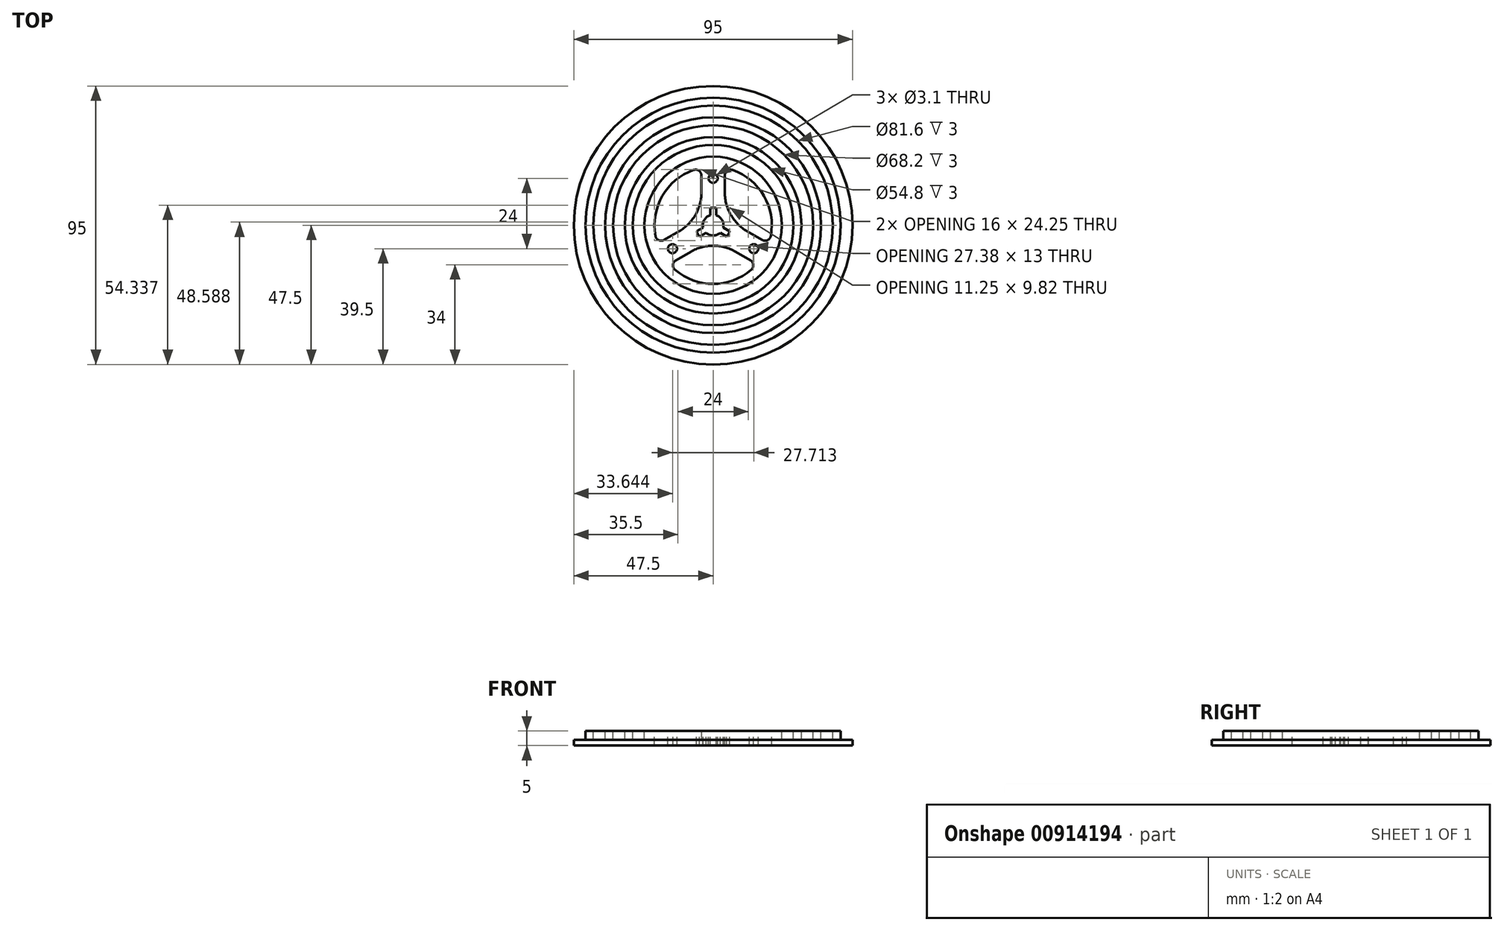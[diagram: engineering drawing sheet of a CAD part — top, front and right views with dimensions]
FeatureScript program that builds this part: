
annotation { "Feature Type Name" : "Feature", "Feature Type Description" : "" }
export const myFeature = defineFeature(function(context is Context, id is Id, definition is map)
    precondition{}
    {
        {
            var Q0;
            Q0=qCreatedBy(makeId("Front.planeOp"),FACE);
            var sketch = newSketch(context, id + "F0", { "sketchPlane" : qUnion([Q0])});
            skLineSegment(sketch, "E0", {"start": v(0, 9.24) * mm, "end": v(0, -8.58) * mm, "construction": true});
            skLineSegment(sketch, "E1", {"start": v(47.5, 0) * mm, "end": v(47.5, 2) * mm});
            skLineSegment(sketch, "E2", {"start": v(47.5, 2) * mm, "end": v(43.5, 2) * mm});
            skLineSegment(sketch, "E3", {"start": v(43.5, 2) * mm, "end": v(43.5, 5) * mm});
            skLineSegment(sketch, "E4", {"start": v(43.5, 5) * mm, "end": v(40.8, 5) * mm});
            skLineSegment(sketch, "E5", {"start": v(40.8, 5) * mm, "end": v(40.8, 2) * mm});
            skLineSegment(sketch, "E6", {"start": v(40.8, 2) * mm, "end": v(36.8, 2) * mm});
            skLineSegment(sketch, "E7", {"start": v(36.8, 2) * mm, "end": v(36.8, 5) * mm});
            skLineSegment(sketch, "E8", {"start": v(36.8, 5) * mm, "end": v(34.1, 5) * mm});
            skLineSegment(sketch, "E9", {"start": v(34.1, 5) * mm, "end": v(34.1, 2) * mm});
            skLineSegment(sketch, "E10", {"start": v(34.1, 2) * mm, "end": v(30.1, 2) * mm});
            skLineSegment(sketch, "E11", {"start": v(30.1, 2) * mm, "end": v(30.1, 5) * mm});
            skLineSegment(sketch, "E12", {"start": v(30.1, 5) * mm, "end": v(27.4, 5) * mm});
            skLineSegment(sketch, "E13", {"start": v(27.4, 5) * mm, "end": v(27.4, 2) * mm});
            skLineSegment(sketch, "E14", {"start": v(27.4, 2) * mm, "end": v(23.4, 2) * mm});
            skLineSegment(sketch, "E15", {"start": v(23.4, 2) * mm, "end": v(23.4, 5) * mm});
            skLineSegment(sketch, "E16", {"start": v(23.4, 5) * mm, "end": v(0, 5) * mm});
            skLineSegment(sketch, "E17", {"start": v(0, 5) * mm, "end": v(0, 0) * mm});
            skLineSegment(sketch, "E18", {"start": v(0, 0) * mm, "end": v(47.5, 0) * mm});
            skSolve(sketch);
        }
        {
            var Q0;
            Q0 = qSketchRegion(id + "F0", true);
            var Q1;
            Q1=sQuery(id+"F0.wireOp",EDGE,"E0");
            revolve(context, id + "F1", {"surfaceOperationType" : NewSurfaceOperationType.NEW, "entities" : qUnion([Q0]), "axis" : qUnion([Q1]), "revolveType" : RevolveType.FULL});
        }
        {
            var Q0;
            Q0=makeQuery(id+"F1.opRevolve","SWEPT_FACE",FACE,{"disambiguationData":[OSD([sQuery(id+"F0.wireOp",EDGE,"E16")])]});
            var sketch = newSketch(context, id + "F2", { "sketchPlane" : qUnion([Q0])});
            skCircle(sketch, "E19", {"center": v(0, 0) * mm, "radius": 3.52 * mm, "construction": true});
            skCircle(sketch, "E20", {"center": v(0, 0) * mm, "radius": 6 * mm, "construction": true});
            skLineSegment(sketch, "E21", {"start": v(1, 3.38) * mm, "end": v(1, 5.92) * mm});
            skLineSegment(sketch, "E22", {"start": v(-1, 3.38) * mm, "end": v(-1, 5.92) * mm});
            skLineSegment(sketch, "E23", {"start": v(0, 22.51) * mm, "end": v(0, 1.14) * mm, "construction": true});
            skArc(sketch, "E24", {"start": v(-1, 5.92) * mm, "mid": v(0, 6) * mm, "end": v(1, 5.92) * mm});
            skLineSegment(sketch, "E25.1.0", {"start": v(-2.43, -2.56) * mm, "end": v(-4.62, -3.82) * mm});
            skLineSegment(sketch, "E25.1.1", {"start": v(-3.43, -0.82) * mm, "end": v(-5.62, -2.1) * mm});
            skLineSegment(sketch, "E25.2.0", {"start": v(3.43, -0.82) * mm, "end": v(5.62, -2.1) * mm});
            skLineSegment(sketch, "E25.2.1", {"start": v(2.43, -2.56) * mm, "end": v(4.62, -3.82) * mm});
            skArc(sketch, "E26", {"start": v(5.62, -2.1) * mm, "mid": v(5.2, -3) * mm, "end": v(4.62, -3.82) * mm});
            skArc(sketch, "E27", {"start": v(-4.62, -3.82) * mm, "mid": v(-5.2, -3) * mm, "end": v(-5.62, -2.1) * mm});
            skArc(sketch, "E28", {"start": v(-3.43, -0.82) * mm, "mid": v(-3.05, 1.76) * mm, "end": v(-1, 3.38) * mm});
            skArc(sketch, "E29", {"start": v(1, 3.38) * mm, "mid": v(3.05, 1.76) * mm, "end": v(3.43, -0.82) * mm});
            skArc(sketch, "E30", {"start": v(2.43, -2.56) * mm, "mid": v(0, -3.52) * mm, "end": v(-2.43, -2.56) * mm});
            skCircle(sketch, "E31", {"center": v(0, 0) * mm, "radius": 7 * mm, "construction": true});
            skCircle(sketch, "E32", {"center": v(0, 0) * mm, "radius": 20 * mm, "construction": true});
            skLineSegment(sketch, "E33", {"start": v(-4, 5.74) * mm, "end": v(-4, 19.6) * mm});
            skLineSegment(sketch, "E34", {"start": v(4, 5.74) * mm, "end": v(4, 19.6) * mm});
            skCircle(sketch, "E35", {"center": v(0, 16) * mm, "radius": 1.55 * mm});
            skPoint(sketch, "E36", {"position": v(-4, 19.6) * mm});
            skPoint(sketch, "E37", {"position": v(4, 19.6) * mm});
            skLineSegment(sketch, "E38.1.0", {"start": v(-2.97, -6.34) * mm, "end": v(-14.97, -13.26) * mm});
            skLineSegment(sketch, "E38.1.1", {"start": v(-6.97, 0.6) * mm, "end": v(-18.97, -6.33) * mm});
            skCircle(sketch, "E38.1.2", {"center": v(-13.86, -8) * mm, "radius": 1.55 * mm});
            skLineSegment(sketch, "E38.2.0", {"start": v(6.97, 0.6) * mm, "end": v(18.97, -6.33) * mm});
            skLineSegment(sketch, "E38.2.1", {"start": v(2.97, -6.34) * mm, "end": v(14.97, -13.26) * mm});
            skCircle(sketch, "E38.2.2", {"center": v(13.86, -8) * mm, "radius": 1.55 * mm});
            skArc(sketch, "E39", {"start": v(4, 19.6) * mm, "mid": v(17.32, 10) * mm, "end": v(18.97, -6.33) * mm});
            skArc(sketch, "E40", {"start": v(-4, 19.6) * mm, "mid": v(-17.32, 10) * mm, "end": v(-18.97, -6.33) * mm});
            skArc(sketch, "E41", {"start": v(-14.97, -13.26) * mm, "mid": v(0, -20) * mm, "end": v(14.97, -13.26) * mm});
            skArc(sketch, "E42", {"start": v(4, 5.74) * mm, "mid": v(6.06, 3.5) * mm, "end": v(6.97, 0.6) * mm});
            skArc(sketch, "E43", {"start": v(2.97, -6.34) * mm, "mid": v(0, -7) * mm, "end": v(-2.97, -6.34) * mm});
            skArc(sketch, "E44", {"start": v(-6.97, 0.6) * mm, "mid": v(-6.06, 3.5) * mm, "end": v(-4, 5.74) * mm});
            skSolve(sketch);
        }
        {
            var Q0;
            Q0 = qSketchRegion(id + "F2", true);
            extrude(context, id + "F3", {"entities" : qUnion([Q0]), "operationType" : NewBodyOperationType.REMOVE, "endBound" : BoundingType.THROUGH_ALL, "oppositeDirection" : true, "depth" : 25 * mm, "offsetDistance" : 25 * mm});
        }
        {
            var Q0;
            Q0=makeQuery(id+"F3.boolean.opBoolean","COPY",EDGE,{"derivedFrom":makeQuery(id+"F3.opExtrude","SWEPT_EDGE",EDGE,{"disambiguationData":[OSD([sQuery(id+"F2.wireOp",EDGE,"E34"),sQuery(id+"F2.wireOp",EDGE,"E42")])]})});
            var Q1;
            Q1=makeQuery(id+"F3.boolean.opBoolean","COPY",EDGE,{"derivedFrom":makeQuery(id+"F3.opExtrude","SWEPT_EDGE",EDGE,{"disambiguationData":[OSD([sQuery(id+"F2.wireOp",EDGE,"E38.2.0"),sQuery(id+"F2.wireOp",EDGE,"E42")])]})});
            var Q2;
            Q2=makeQuery(id+"F3.boolean.opBoolean","COPY",EDGE,{"derivedFrom":makeQuery(id+"F3.opExtrude","SWEPT_EDGE",EDGE,{"disambiguationData":[OSD([sQuery(id+"F2.wireOp",EDGE,"E38.1.0"),sQuery(id+"F2.wireOp",EDGE,"E43")])]})});
            var Q3;
            Q3=makeQuery(id+"F3.boolean.opBoolean","COPY",EDGE,{"derivedFrom":makeQuery(id+"F3.opExtrude","SWEPT_EDGE",EDGE,{"disambiguationData":[OSD([sQuery(id+"F2.wireOp",EDGE,"E38.2.1"),sQuery(id+"F2.wireOp",EDGE,"E43")])]})});
            var Q4;
            Q4=makeQuery(id+"F3.boolean.opBoolean","COPY",EDGE,{"derivedFrom":makeQuery(id+"F3.opExtrude","SWEPT_EDGE",EDGE,{"disambiguationData":[OSD([sQuery(id+"F2.wireOp",EDGE,"E33"),sQuery(id+"F2.wireOp",EDGE,"E44")])]})});
            var Q5;
            Q5=makeQuery(id+"F3.boolean.opBoolean","COPY",EDGE,{"derivedFrom":makeQuery(id+"F3.opExtrude","SWEPT_EDGE",EDGE,{"disambiguationData":[OSD([sQuery(id+"F2.wireOp",EDGE,"E38.1.1"),sQuery(id+"F2.wireOp",EDGE,"E44")])]})});
            fillet(context, id + "F4", {"entities" : qUnion([Q0, Q1, Q2, Q3, Q4, Q5]), "radius" : 15 * mm, "tangentPropagation" : true, "allowEdgeOverflow" : false});
        }
        {
            var Q0;
            Q0=makeQuery(id+"F3.boolean.opBoolean","COPY",EDGE,{"derivedFrom":makeQuery(id+"F3.opExtrude","SWEPT_EDGE",EDGE,{"disambiguationData":[OSD([sQuery(id+"F2.wireOp",EDGE,"E33"),sQuery(id+"F2.wireOp",EDGE,"E40")])]})});
            var Q1;
            Q1=makeQuery(id+"F3.boolean.opBoolean","COPY",EDGE,{"derivedFrom":makeQuery(id+"F3.opExtrude","SWEPT_EDGE",EDGE,{"disambiguationData":[OSD([sQuery(id+"F2.wireOp",EDGE,"E34"),sQuery(id+"F2.wireOp",EDGE,"E39")])]})});
            var Q2;
            Q2=makeQuery(id+"F3.boolean.opBoolean","COPY",EDGE,{"derivedFrom":makeQuery(id+"F3.opExtrude","SWEPT_EDGE",EDGE,{"disambiguationData":[OSD([sQuery(id+"F2.wireOp",EDGE,"E38.1.1"),sQuery(id+"F2.wireOp",EDGE,"E40")])]})});
            var Q3;
            Q3=makeQuery(id+"F3.boolean.opBoolean","COPY",EDGE,{"derivedFrom":makeQuery(id+"F3.opExtrude","SWEPT_EDGE",EDGE,{"disambiguationData":[OSD([sQuery(id+"F2.wireOp",EDGE,"E38.1.0"),sQuery(id+"F2.wireOp",EDGE,"E41")])]})});
            var Q4;
            Q4=makeQuery(id+"F3.boolean.opBoolean","COPY",EDGE,{"derivedFrom":makeQuery(id+"F3.opExtrude","SWEPT_EDGE",EDGE,{"disambiguationData":[OSD([sQuery(id+"F2.wireOp",EDGE,"E38.2.1"),sQuery(id+"F2.wireOp",EDGE,"E41")])]})});
            var Q5;
            Q5=makeQuery(id+"F3.boolean.opBoolean","COPY",EDGE,{"derivedFrom":makeQuery(id+"F3.opExtrude","SWEPT_EDGE",EDGE,{"disambiguationData":[OSD([sQuery(id+"F2.wireOp",EDGE,"E38.2.0"),sQuery(id+"F2.wireOp",EDGE,"E39")])]})});
            fillet(context, id + "F5", {"entities" : qUnion([Q0, Q1, Q2, Q3, Q4, Q5]), "radius" : 2 * mm, "tangentPropagation" : true, "allowEdgeOverflow" : false});
        }
    });
